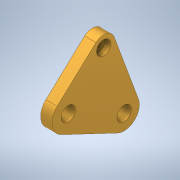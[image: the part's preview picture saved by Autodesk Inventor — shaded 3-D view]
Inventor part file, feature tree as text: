
AUTODESK INVENTOR PART (.ipt)
format: ipt  version: 2020 (Build 240168000, 168)  size: 151,552 bytes
history: native  units: in
note: dims shown in document units (in); Inventor stores cm internally (conversion verified against a paired STEP export)
features: extrude x3, sketch x3, projected_geometry x1
ambient origin geometry x8: Origin, YZ Plane, XZ Plane, XY Plane, X Axis, Y Axis, Z Axis, Center Point
bodies: Solid1 (feature_tree)
feature tree (7):
  extrude  "Extrusion1"  Depth=0.4523in
  extrude  "Extrusion2"  Depth=0.2118in
  extrude  "Extrusion3"  Depth=0.1575in TaperAngle=0.0deg
  sketch  "Sketch1"  dims[d0=0.2008in d1=0.2008in d3=0.4523in]
  sketch  "Sketch2"  dims[d4=0.2118in d5=0.8586in]
  projected_geometry  "Projected Loop1"
  sketch  "Sketch3"  dims[d6=0.8656in d7=0.1575in d8=0.0in d11=0.0787in d12=0.315in d13=0.1575in d14=0.0in d15=0.1969in d16=0.0787in d17=0.0in d20=0.7087in d21=0.4228in]
